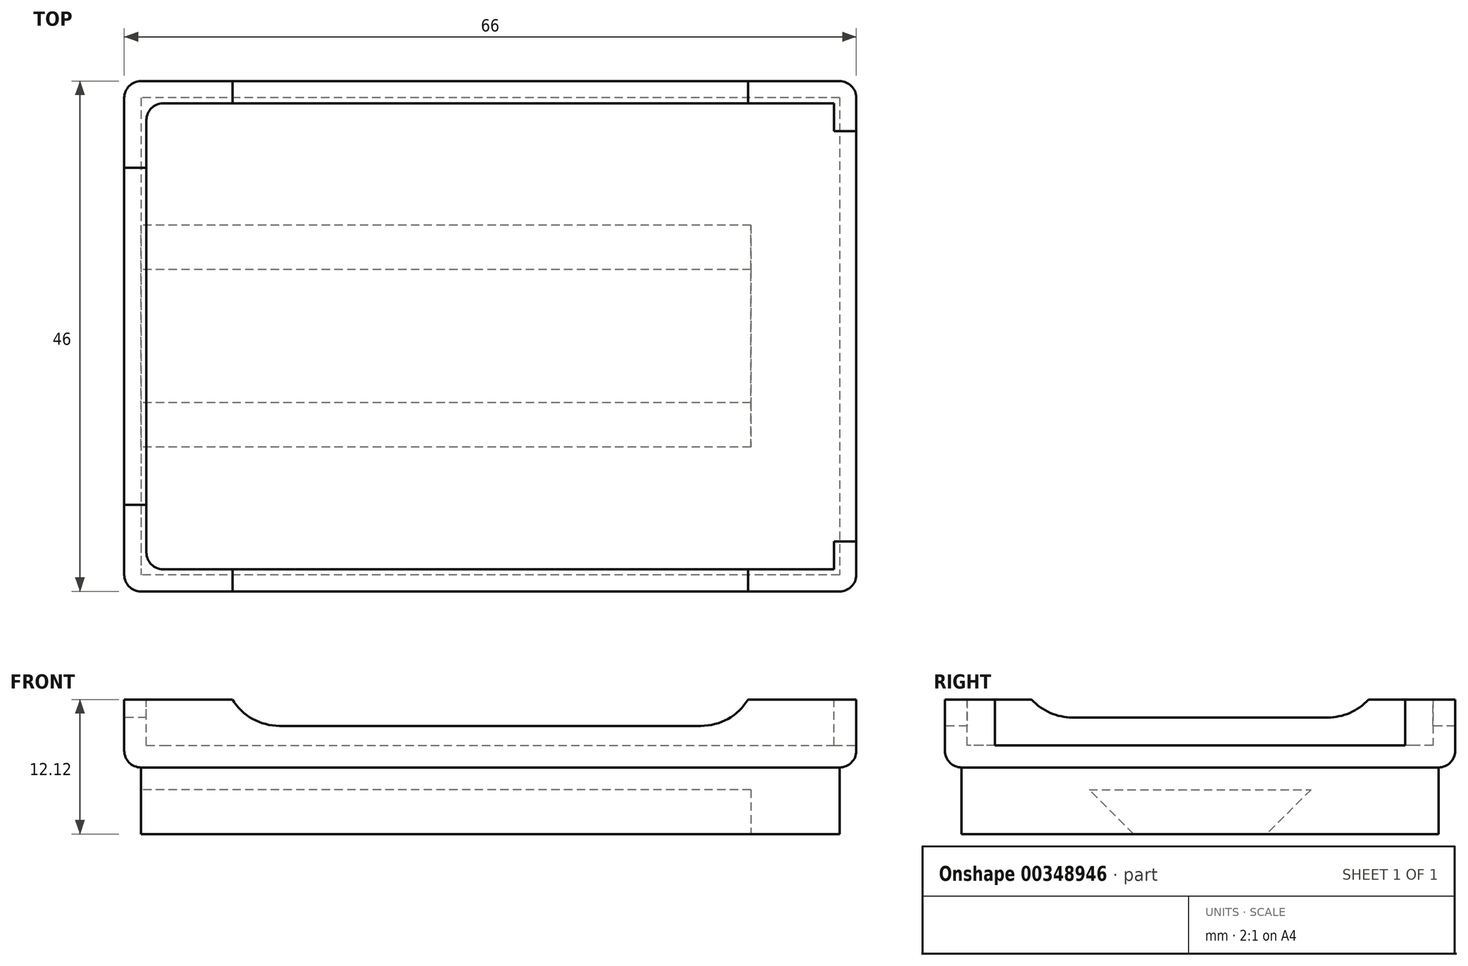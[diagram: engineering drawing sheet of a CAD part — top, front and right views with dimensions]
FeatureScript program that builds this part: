
annotation { "Feature Type Name" : "Feature", "Feature Type Description" : "" }
export const myFeature = defineFeature(function(context is Context, id is Id, definition is map)
    precondition{}
    {
        {
            var Q0;
            Q0=qCreatedBy(makeId("Top.planeOp"),FACE);
            var sketch = newSketch(context, id + "F0", { "sketchPlane" : qUnion([Q0])});
            skLineSegment(sketch, "E0.bottom", {"start": v(33, 23) * mm, "end": v(-33, 23) * mm});
            skLineSegment(sketch, "E0.top", {"start": v(33, -23) * mm, "end": v(-33, -23) * mm});
            skLineSegment(sketch, "E0.left", {"start": v(33, 23) * mm, "end": v(33, -23) * mm});
            skLineSegment(sketch, "E0.right", {"start": v(-33, 23) * mm, "end": v(-33, -23) * mm});
            skPoint(sketch, "E0.middle", {"position": v(0, 0) * mm});
            skSolve(sketch);
        }
        {
            var Q0;
            Q0=makeQuery(id+"F0.imprint","IMPRINT",FACE,{"disambiguationData":[TD([[makeQuery(id+"F0.imprint","IMPRINT",EDGE,{"derivedFrom":sQuery(id+"F0.wireOp",EDGE,"E0.bottom")}),1.0]])]});
            extrude(context, id + "F1", {"entities" : qUnion([Q0]), "depth" : 11.5 * mm});
        }
        {
            var Q0;
            Q0=makeQuery(id+"F1.opExtrude","CAP_EDGE",EDGE,{"disambiguationData":[OSD([sQuery(id+"F0.wireOp",EDGE,"E0.right")])],"isStart":false});
            var Q1;
            Q1=makeQuery(id+"F1.opExtrude","CAP_EDGE",EDGE,{"disambiguationData":[OSD([sQuery(id+"F0.wireOp",EDGE,"E0.top")])],"isStart":false});
            var Q2;
            Q2=makeQuery(id+"F1.opExtrude","CAP_EDGE",EDGE,{"disambiguationData":[OSD([sQuery(id+"F0.wireOp",EDGE,"E0.left")])],"isStart":false});
            var Q3;
            Q3=makeQuery(id+"F1.opExtrude","CAP_EDGE",EDGE,{"disambiguationData":[OSD([sQuery(id+"F0.wireOp",EDGE,"E0.bottom")])],"isStart":false});
            var Q4;
            Q4=makeQuery(id+"F1.opExtrude","SWEPT_EDGE",EDGE,{"disambiguationData":[OSD([sQuery(id+"F0.wireOp",EDGE,"E0.top"),sQuery(id+"F0.wireOp",EDGE,"E0.left")])]});
            var Q5;
            Q5=makeQuery(id+"F1.opExtrude","SWEPT_EDGE",EDGE,{"disambiguationData":[OSD([sQuery(id+"F0.wireOp",EDGE,"E0.bottom"),sQuery(id+"F0.wireOp",EDGE,"E0.left")])]});
            var Q6;
            Q6=makeQuery(id+"F1.opExtrude","SWEPT_EDGE",EDGE,{"disambiguationData":[OSD([sQuery(id+"F0.wireOp",EDGE,"E0.top"),sQuery(id+"F0.wireOp",EDGE,"E0.right")])]});
            var Q7;
            Q7=makeQuery(id+"F1.opExtrude","SWEPT_EDGE",EDGE,{"disambiguationData":[OSD([sQuery(id+"F0.wireOp",EDGE,"E0.bottom"),sQuery(id+"F0.wireOp",EDGE,"E0.right")])]});
            fillet(context, id + "F2", {"entities" : qUnion([Q0, Q1, Q2, Q3, Q4, Q5, Q6, Q7]), "radius" : 1.5 * mm, "tangentPropagation" : true, "allowEdgeOverflow" : false});
        }
        {
            var Q0;
            Q0=makeQuery(id+"F1.opExtrude","CAP_FACE",FACE,{"disambiguationData":[OSD([sQuery(id+"F0.wireOp",EDGE,"E0.bottom"),sQuery(id+"F0.wireOp",EDGE,"E0.top"),sQuery(id+"F0.wireOp",EDGE,"E0.left"),sQuery(id+"F0.wireOp",EDGE,"E0.right")])],"isStart":true});
            shell(context, id + "F3", {"entities" : qUnion([Q0]), "thickness" : 2 * mm});
        }
        {
            var Q0;
            Q0=makeQuery(id+"F3.opShell","OFFSET_EDGE",EDGE,{"disambiguationData":[OSD([sQuery(id+"F0.wireOp",EDGE,"E0.bottom"),sQuery(id+"F0.wireOp",EDGE,"E0.right")])]});
            var Q1;
            Q1=makeQuery(id+"F3.opShell","OFFSET_EDGE",EDGE,{"disambiguationData":[OSD([sQuery(id+"F0.wireOp",EDGE,"E0.top"),sQuery(id+"F0.wireOp",EDGE,"E0.right")])]});
            fillet(context, id + "F4", {"entities" : qUnion([Q0, Q1]), "radius" : 1.5 * mm, "tangentPropagation" : true, "allowEdgeOverflow" : false});
        }
        {
            var Q0;
            Q0=makeQuery(id+"F1.opExtrude","SWEPT_BODY",BODY,{"disambiguationData":[OSD([sQuery(id+"F0.wireOp",EDGE,"E0.bottom"),sQuery(id+"F0.wireOp",EDGE,"E0.top"),sQuery(id+"F0.wireOp",EDGE,"E0.left"),sQuery(id+"F0.wireOp",EDGE,"E0.right")])]});
            var Q1;
            Q1=qCreatedBy(makeId("Top.planeOp"),FACE);
            mirror(context, id + "F5", {"operationType" : NewBodyOperationType.ADD, "entities" : qUnion([Q0]), "mirrorPlane" : qUnion([Q1])});
        }
        {
            var Q0;
            {var subQ0=makeQuery(id+"F1.opExtrude","SWEPT_FACE",FACE,{"disambiguationData":[OSD([sQuery(id+"F0.wireOp",EDGE,"E0.top")])]});Q0=makeQuery(id+"F5.boolean.opBoolean","MERGE",FACE,{"derivedFrom":[subQ0,makeQuery(id+"F5.opPattern","COPY",FACE,{"derivedFrom":subQ0,"instanceName":"1"})]});}
            var sketch = newSketch(context, id + "F6", { "sketchPlane" : qUnion([Q0])});
            skLineSegment(sketch, "E1.bottom", {"start": v(24, -7.75) * mm, "end": v(-24, -7.75) * mm});
            skLineSegment(sketch, "E1.top", {"start": v(24, 7.75) * mm, "end": v(-24, 7.75) * mm});
            skLineSegment(sketch, "E1.left", {"start": v(24, -7.75) * mm, "end": v(24, 7.75) * mm});
            skLineSegment(sketch, "E1.right", {"start": v(-24, -7.75) * mm, "end": v(-24, 7.75) * mm});
            skPoint(sketch, "E1.middle", {"position": v(0, 0) * mm});
            skSolve(sketch);
        }
        {
            var Q0;
            Q0=makeQuery(id+"F6.imprint","IMPRINT",FACE,{"disambiguationData":[TD([[makeQuery(id+"F6.imprint","IMPRINT",EDGE,{"derivedFrom":sQuery(id+"F6.wireOp",EDGE,"E1.bottom")}),-1.0]])]});
            extrude(context, id + "F7", {"entities" : qUnion([Q0]), "operationType" : NewBodyOperationType.REMOVE, "endBound" : BoundingType.THROUGH_ALL, "oppositeDirection" : true, "depth" : 5 * mm});
        }
        {
            var Q0;
            {var subQ0=makeQuery(id+"F1.opExtrude","SWEPT_FACE",FACE,{"disambiguationData":[OSD([sQuery(id+"F0.wireOp",EDGE,"E0.right")])]});Q0=makeQuery(id+"F5.boolean.opBoolean","MERGE",FACE,{"derivedFrom":[subQ0,makeQuery(id+"F5.opPattern","COPY",FACE,{"derivedFrom":subQ0,"instanceName":"1"})]});}
            var sketch = newSketch(context, id + "F8", { "sketchPlane" : qUnion([Q0])});
            skLineSegment(sketch, "E2.bottom", {"start": v(16.5, 7) * mm, "end": v(-16.5, 7) * mm});
            skLineSegment(sketch, "E2.top", {"start": v(16.5, -7) * mm, "end": v(-16.5, -7) * mm});
            skLineSegment(sketch, "E2.left", {"start": v(16.5, 7) * mm, "end": v(16.5, -7) * mm});
            skLineSegment(sketch, "E2.right", {"start": v(-16.5, 7) * mm, "end": v(-16.5, -7) * mm});
            skPoint(sketch, "E2.middle", {"position": v(0, 0) * mm});
            skSolve(sketch);
        }
        {
            var Q0;
            Q0=makeQuery(id+"F8.imprint","IMPRINT",FACE,{"disambiguationData":[TD([[makeQuery(id+"F8.imprint","IMPRINT",EDGE,{"derivedFrom":sQuery(id+"F8.wireOp",EDGE,"E2.bottom")}),1.0]])]});
            extrude(context, id + "F9", {"entities" : qUnion([Q0]), "operationType" : NewBodyOperationType.REMOVE, "oppositeDirection" : true, "depth" : 5 * mm});
        }
        {
            var Q0;
            {var subQ0=sQuery(id+"F0.wireOp",EDGE,"E0.left");var subQ2=makeQuery(id+"F1.opExtrude","SWEPT_FACE",FACE,{"disambiguationData":[OSD([subQ0])]});var subQ3=sQuery(id+"F8.wireOp",EDGE,"E2.right");var subQ4=sQuery(id+"F8.wireOp",EDGE,"E2.top");Q0=makeQuery(id+"F9.boolean.opBoolean","COPY",EDGE,{"disambiguationData":[TD([subQ2])],"derivedFrom":makeQuery(id+"F9.opExtrude","SWEPT_EDGE",EDGE,{"disambiguationData":[OSD([subQ4,subQ3])]})});}
            var Q1;
            {var subQ0=sQuery(id+"F0.wireOp",EDGE,"E0.right");var subQ2=makeQuery(id+"F1.opExtrude","SWEPT_FACE",FACE,{"disambiguationData":[OSD([subQ0])]});var subQ3=sQuery(id+"F8.wireOp",EDGE,"E2.top");var subQ4=sQuery(id+"F8.wireOp",EDGE,"E2.right");Q1=makeQuery(id+"F9.boolean.opBoolean","COPY",EDGE,{"disambiguationData":[TD([subQ2])],"derivedFrom":makeQuery(id+"F9.opExtrude","SWEPT_EDGE",EDGE,{"disambiguationData":[OSD([subQ3,subQ4])]})});}
            var Q2;
            {var subQ0=sQuery(id+"F0.wireOp",EDGE,"E0.left");var subQ2=makeQuery(id+"F1.opExtrude","SWEPT_FACE",FACE,{"disambiguationData":[OSD([subQ0])]});var subQ3=sQuery(id+"F8.wireOp",EDGE,"E2.top");var subQ4=sQuery(id+"F8.wireOp",EDGE,"E2.left");Q2=makeQuery(id+"F9.boolean.opBoolean","COPY",EDGE,{"disambiguationData":[TD([subQ2])],"derivedFrom":makeQuery(id+"F9.opExtrude","SWEPT_EDGE",EDGE,{"disambiguationData":[OSD([subQ3,subQ4])]})});}
            var Q3;
            {var subQ0=sQuery(id+"F0.wireOp",EDGE,"E0.right");var subQ2=makeQuery(id+"F1.opExtrude","SWEPT_FACE",FACE,{"disambiguationData":[OSD([subQ0])]});var subQ3=sQuery(id+"F8.wireOp",EDGE,"E2.top");var subQ4=sQuery(id+"F8.wireOp",EDGE,"E2.left");Q3=makeQuery(id+"F9.boolean.opBoolean","COPY",EDGE,{"disambiguationData":[TD([subQ2])],"derivedFrom":makeQuery(id+"F9.opExtrude","SWEPT_EDGE",EDGE,{"disambiguationData":[OSD([subQ3,subQ4])]})});}
            var Q4;
            {var subQ0=sQuery(id+"F0.wireOp",EDGE,"E0.left");var subQ2=makeQuery(id+"F1.opExtrude","SWEPT_FACE",FACE,{"disambiguationData":[OSD([subQ0])]});var subQ3=sQuery(id+"F8.wireOp",EDGE,"E2.right");var subQ4=sQuery(id+"F8.wireOp",EDGE,"E2.bottom");Q4=makeQuery(id+"F9.boolean.opBoolean","COPY",EDGE,{"disambiguationData":[TD([subQ2])],"derivedFrom":makeQuery(id+"F9.opExtrude","SWEPT_EDGE",EDGE,{"disambiguationData":[OSD([subQ4,subQ3])]})});}
            var Q5;
            {var subQ0=sQuery(id+"F0.wireOp",EDGE,"E0.right");var subQ2=makeQuery(id+"F1.opExtrude","SWEPT_FACE",FACE,{"disambiguationData":[OSD([subQ0])]});var subQ3=sQuery(id+"F8.wireOp",EDGE,"E2.bottom");var subQ4=sQuery(id+"F8.wireOp",EDGE,"E2.right");Q5=makeQuery(id+"F9.boolean.opBoolean","COPY",EDGE,{"disambiguationData":[TD([subQ2])],"derivedFrom":makeQuery(id+"F9.opExtrude","SWEPT_EDGE",EDGE,{"disambiguationData":[OSD([subQ3,subQ4])]})});}
            var Q6;
            {var subQ0=sQuery(id+"F0.wireOp",EDGE,"E0.right");var subQ2=sQuery(id+"F8.wireOp",EDGE,"E2.bottom");var subQ3=makeQuery(id+"F1.opExtrude","SWEPT_FACE",FACE,{"disambiguationData":[OSD([subQ0])]});var subQ4=sQuery(id+"F8.wireOp",EDGE,"E2.left");Q6=makeQuery(id+"F9.boolean.opBoolean","COPY",EDGE,{"disambiguationData":[TD([subQ3])],"derivedFrom":makeQuery(id+"F9.opExtrude","SWEPT_EDGE",EDGE,{"disambiguationData":[OSD([subQ2,subQ4])]})});}
            var Q7;
            {var subQ0=sQuery(id+"F0.wireOp",EDGE,"E0.left");var subQ2=makeQuery(id+"F1.opExtrude","SWEPT_FACE",FACE,{"disambiguationData":[OSD([subQ0])]});var subQ3=sQuery(id+"F8.wireOp",EDGE,"E2.bottom");var subQ4=sQuery(id+"F8.wireOp",EDGE,"E2.left");Q7=makeQuery(id+"F9.boolean.opBoolean","COPY",EDGE,{"disambiguationData":[TD([subQ2])],"derivedFrom":makeQuery(id+"F9.opExtrude","SWEPT_EDGE",EDGE,{"disambiguationData":[OSD([subQ3,subQ4])]})});}
            fillet(context, id + "F10", {"entities" : qUnion([Q0, Q1, Q2, Q3, Q4, Q5, Q6, Q7]), "radius" : 5 * mm, "tangentPropagation" : true, "allowEdgeOverflow" : false});
        }
        {
            var Q0;
            {var subQ0=sQuery(id+"F0.wireOp",EDGE,"E0.top");var subQ2=makeQuery(id+"F1.opExtrude","SWEPT_FACE",FACE,{"disambiguationData":[OSD([subQ0])]});var subQ3=sQuery(id+"F6.wireOp",EDGE,"E1.top");var subQ4=sQuery(id+"F6.wireOp",EDGE,"E1.right");Q0=makeQuery(id+"F7.boolean.opBoolean","COPY",EDGE,{"disambiguationData":[TD([subQ2])],"derivedFrom":makeQuery(id+"F7.opExtrude","SWEPT_EDGE",EDGE,{"disambiguationData":[OSD([subQ3,subQ4])]})});}
            var Q1;
            {var subQ0=sQuery(id+"F0.wireOp",EDGE,"E0.top");var subQ2=makeQuery(id+"F1.opExtrude","SWEPT_FACE",FACE,{"disambiguationData":[OSD([subQ0])]});var subQ3=sQuery(id+"F6.wireOp",EDGE,"E1.left");var subQ4=sQuery(id+"F6.wireOp",EDGE,"E1.top");Q1=makeQuery(id+"F7.boolean.opBoolean","COPY",EDGE,{"disambiguationData":[TD([subQ2])],"derivedFrom":makeQuery(id+"F7.opExtrude","SWEPT_EDGE",EDGE,{"disambiguationData":[OSD([subQ4,subQ3])]})});}
            var Q2;
            {var subQ0=sQuery(id+"F0.wireOp",EDGE,"E0.top");var subQ2=sQuery(id+"F6.wireOp",EDGE,"E1.bottom");var subQ3=makeQuery(id+"F1.opExtrude","SWEPT_FACE",FACE,{"disambiguationData":[OSD([subQ0])]});var subQ4=sQuery(id+"F6.wireOp",EDGE,"E1.right");Q2=makeQuery(id+"F7.boolean.opBoolean","COPY",EDGE,{"disambiguationData":[TD([subQ3])],"derivedFrom":makeQuery(id+"F7.opExtrude","SWEPT_EDGE",EDGE,{"disambiguationData":[OSD([subQ2,subQ4])]})});}
            var Q3;
            {var subQ0=sQuery(id+"F0.wireOp",EDGE,"E0.top");var subQ2=sQuery(id+"F6.wireOp",EDGE,"E1.bottom");var subQ3=makeQuery(id+"F1.opExtrude","SWEPT_FACE",FACE,{"disambiguationData":[OSD([subQ0])]});var subQ4=sQuery(id+"F6.wireOp",EDGE,"E1.left");Q3=makeQuery(id+"F7.boolean.opBoolean","COPY",EDGE,{"disambiguationData":[TD([subQ3])],"derivedFrom":makeQuery(id+"F7.opExtrude","SWEPT_EDGE",EDGE,{"disambiguationData":[OSD([subQ2,subQ4])]})});}
            fillet(context, id + "F11", {"entities" : qUnion([Q0, Q1, Q2, Q3]), "radius" : 5 * mm, "tangentPropagation" : true, "allowEdgeOverflow" : false});
        }
        {
            var Q0;
            {var subQ0=sQuery(id+"F0.wireOp",EDGE,"E0.bottom");var subQ1=makeQuery(id+"F1.opExtrude","SWEPT_FACE",FACE,{"disambiguationData":[OSD([subQ0])]});var subQ3=sQuery(id+"F6.wireOp",EDGE,"E1.top");var subQ4=sQuery(id+"F6.wireOp",EDGE,"E1.left");Q0=makeQuery(id+"F7.boolean.opBoolean","COPY",EDGE,{"disambiguationData":[TD([subQ1])],"derivedFrom":makeQuery(id+"F7.opExtrude","SWEPT_EDGE",EDGE,{"disambiguationData":[OSD([subQ3,subQ4])]})});}
            var Q1;
            {var subQ0=sQuery(id+"F0.wireOp",EDGE,"E0.bottom");var subQ1=makeQuery(id+"F1.opExtrude","SWEPT_FACE",FACE,{"disambiguationData":[OSD([subQ0])]});var subQ3=sQuery(id+"F6.wireOp",EDGE,"E1.bottom");var subQ4=sQuery(id+"F6.wireOp",EDGE,"E1.left");Q1=makeQuery(id+"F7.boolean.opBoolean","COPY",EDGE,{"disambiguationData":[TD([subQ1])],"derivedFrom":makeQuery(id+"F7.opExtrude","SWEPT_EDGE",EDGE,{"disambiguationData":[OSD([subQ3,subQ4])]})});}
            var Q2;
            {var subQ0=sQuery(id+"F0.wireOp",EDGE,"E0.bottom");var subQ1=makeQuery(id+"F1.opExtrude","SWEPT_FACE",FACE,{"disambiguationData":[OSD([subQ0])]});var subQ3=sQuery(id+"F6.wireOp",EDGE,"E1.right");var subQ4=sQuery(id+"F6.wireOp",EDGE,"E1.bottom");Q2=makeQuery(id+"F7.boolean.opBoolean","COPY",EDGE,{"disambiguationData":[TD([subQ1])],"derivedFrom":makeQuery(id+"F7.opExtrude","SWEPT_EDGE",EDGE,{"disambiguationData":[OSD([subQ4,subQ3])]})});}
            var Q3;
            {var subQ0=sQuery(id+"F0.wireOp",EDGE,"E0.bottom");var subQ1=makeQuery(id+"F1.opExtrude","SWEPT_FACE",FACE,{"disambiguationData":[OSD([subQ0])]});var subQ3=sQuery(id+"F6.wireOp",EDGE,"E1.right");var subQ4=sQuery(id+"F6.wireOp",EDGE,"E1.top");Q3=makeQuery(id+"F7.boolean.opBoolean","COPY",EDGE,{"disambiguationData":[TD([subQ1])],"derivedFrom":makeQuery(id+"F7.opExtrude","SWEPT_EDGE",EDGE,{"disambiguationData":[OSD([subQ4,subQ3])]})});}
            fillet(context, id + "F12", {"entities" : qUnion([Q0, Q1, Q2, Q3]), "radius" : 5 * mm, "tangentPropagation" : true, "allowEdgeOverflow" : false});
        }
        {
            var Q0;
            Q0=makeQuery(id+"F1.opExtrude","CAP_FACE",FACE,{"disambiguationData":[OSD([sQuery(id+"F0.wireOp",EDGE,"E0.bottom"),sQuery(id+"F0.wireOp",EDGE,"E0.top"),sQuery(id+"F0.wireOp",EDGE,"E0.left"),sQuery(id+"F0.wireOp",EDGE,"E0.right")])],"isStart":false});
            var sketch = newSketch(context, id + "F13", { "sketchPlane" : qUnion([Q0])});
            skLineSegment(sketch, "E3.bottom", {"start": v(20, -10) * mm, "end": v(-20, -10) * mm});
            skLineSegment(sketch, "E3.top", {"start": v(20, 10) * mm, "end": v(-20, 10) * mm});
            skLineSegment(sketch, "E3.left", {"start": v(20, -10) * mm, "end": v(20, 10) * mm});
            skLineSegment(sketch, "E3.right", {"start": v(-20, -10) * mm, "end": v(-20, 10) * mm});
            skPoint(sketch, "E3.middle", {"position": v(0, 0) * mm});
            skSolve(sketch);
        }
        {
            var Q0;
            Q0=makeQuery(id+"F13.imprint","IMPRINT",FACE,{"disambiguationData":[TD([[makeQuery(id+"F13.imprint","IMPRINT",EDGE,{"derivedFrom":sQuery(id+"F13.wireOp",EDGE,"E3.bottom")}),-1.0]])]});
            extrude(context, id + "F14", {"entities" : qUnion([Q0]), "operationType" : NewBodyOperationType.REMOVE, "oppositeDirection" : true, "depth" : 5 * mm});
        }
        {
            var Q0;
            Q0=makeQuery(id+"F14.boolean.opBoolean","COPY",EDGE,{"derivedFrom":makeQuery(id+"F14.opExtrude","SWEPT_EDGE",EDGE,{"disambiguationData":[OSD([sQuery(id+"F13.wireOp",EDGE,"E3.top"),sQuery(id+"F13.wireOp",EDGE,"E3.right")])]})});
            var Q1;
            Q1=makeQuery(id+"F14.boolean.opBoolean","COPY",EDGE,{"derivedFrom":makeQuery(id+"F14.opExtrude","SWEPT_EDGE",EDGE,{"disambiguationData":[OSD([sQuery(id+"F13.wireOp",EDGE,"E3.bottom"),sQuery(id+"F13.wireOp",EDGE,"E3.right")])]})});
            var Q2;
            Q2=makeQuery(id+"F14.boolean.opBoolean","COPY",EDGE,{"derivedFrom":makeQuery(id+"F14.opExtrude","SWEPT_EDGE",EDGE,{"disambiguationData":[OSD([sQuery(id+"F13.wireOp",EDGE,"E3.bottom"),sQuery(id+"F13.wireOp",EDGE,"E3.left")])]})});
            var Q3;
            Q3=makeQuery(id+"F14.boolean.opBoolean","COPY",EDGE,{"derivedFrom":makeQuery(id+"F14.opExtrude","SWEPT_EDGE",EDGE,{"disambiguationData":[OSD([sQuery(id+"F13.wireOp",EDGE,"E3.top"),sQuery(id+"F13.wireOp",EDGE,"E3.left")])]})});
            fillet(context, id + "F15", {"entities" : qUnion([Q0, Q1, Q2, Q3]), "radius" : 5 * mm, "tangentPropagation" : true, "allowEdgeOverflow" : false});
        }
        {
            var Q0;
            {var subQ0=makeQuery(id+"F1.opExtrude","SWEPT_FACE",FACE,{"disambiguationData":[OSD([sQuery(id+"F0.wireOp",EDGE,"E0.left")])]});Q0=makeQuery(id+"F5.boolean.opBoolean","MERGE",FACE,{"derivedFrom":[subQ0,makeQuery(id+"F5.opPattern","COPY",FACE,{"derivedFrom":subQ0,"instanceName":"1"})]});}
            var sketch = newSketch(context, id + "F16", { "sketchPlane" : qUnion([Q0])});
            skLineSegment(sketch, "E4.bottom", {"start": v(18.5, -9.5) * mm, "end": v(-18.5, -9.5) * mm});
            skLineSegment(sketch, "E4.top", {"start": v(18.5, 9.5) * mm, "end": v(-18.5, 9.5) * mm});
            skLineSegment(sketch, "E4.left", {"start": v(18.5, -9.5) * mm, "end": v(18.5, 9.5) * mm});
            skLineSegment(sketch, "E4.right", {"start": v(-18.5, -9.5) * mm, "end": v(-18.5, 9.5) * mm});
            skPoint(sketch, "E4.middle", {"position": v(0, 0) * mm});
            skSolve(sketch);
        }
        {
            var Q0;
            Q0=makeQuery(id+"F16.imprint","IMPRINT",FACE,{"disambiguationData":[TD([[makeQuery(id+"F16.imprint","IMPRINT",EDGE,{"derivedFrom":sQuery(id+"F16.wireOp",EDGE,"E4.bottom")}),-1.0]])]});
            extrude(context, id + "F17", {"entities" : qUnion([Q0]), "operationType" : NewBodyOperationType.REMOVE, "oppositeDirection" : true, "depth" : 5 * mm});
        }
        {
            var Q0;
            Q0=makeQuery(id+"F5.opPattern","COPY",FACE,{"derivedFrom":makeQuery(id+"F1.opExtrude","CAP_FACE",FACE,{"disambiguationData":[OSD([sQuery(id+"F0.wireOp",EDGE,"E0.bottom"),sQuery(id+"F0.wireOp",EDGE,"E0.top"),sQuery(id+"F0.wireOp",EDGE,"E0.left"),sQuery(id+"F0.wireOp",EDGE,"E0.right")])],"isStart":false}),"instanceName":"1"});
            var sketch = newSketch(context, id + "F18", { "sketchPlane" : qUnion([Q0])});
            skLineSegment(sketch, "E5.bottom", {"start": v(31.5, -21.5) * mm, "end": v(-31.5, -21.5) * mm});
            skLineSegment(sketch, "E5.top", {"start": v(31.5, 21.5) * mm, "end": v(-31.5, 21.5) * mm});
            skLineSegment(sketch, "E5.left", {"start": v(31.5, -21.5) * mm, "end": v(31.5, 21.5) * mm});
            skLineSegment(sketch, "E5.right", {"start": v(-31.5, -21.5) * mm, "end": v(-31.5, 21.5) * mm});
            skPoint(sketch, "E5.middle", {"position": v(0, 0) * mm});
            skSolve(sketch);
        }
        {
            var Q0;
            Q0=makeQuery(id+"F18.imprint","IMPRINT",FACE,{"disambiguationData":[TD([[makeQuery(id+"F18.imprint","IMPRINT",EDGE,{"derivedFrom":sQuery(id+"F18.wireOp",EDGE,"E5.bottom")}),-1.0]])]});
            extrude(context, id + "F19", {"entities" : qUnion([Q0]), "operationType" : NewBodyOperationType.ADD, "depth" : 6 * mm});
        }
        {
            var Q0;
            Q0=makeQuery(id+"F19.opExtrude","SWEPT_FACE",FACE,{"disambiguationData":[OSD([sQuery(id+"F18.wireOp",EDGE,"E5.right")])]});
            var sketch = newSketch(context, id + "F20", { "sketchPlane" : qUnion([Q0])});
            skLineSegment(sketch, "E6.bottom", {"start": v(10, -21.5) * mm, "end": v(-10, -21.5) * mm, "construction": true});
            skLineSegment(sketch, "E6.top", {"start": v(10, -13.5) * mm, "end": v(-10, -13.5) * mm, "construction": true});
            skLineSegment(sketch, "E6.left", {"start": v(10, -21.5) * mm, "end": v(10, -13.5) * mm, "construction": true});
            skLineSegment(sketch, "E6.right", {"start": v(-10, -21.5) * mm, "end": v(-10, -13.5) * mm, "construction": true});
            skPoint(sketch, "E6.middle", {"position": v(0, -17.5) * mm});
            skLineSegment(sketch, "E7.bottom", {"start": v(6, -21.5) * mm, "end": v(-6, -21.5) * mm, "construction": true});
            skLineSegment(sketch, "E7.top", {"start": v(6, -13.5) * mm, "end": v(-6, -13.5) * mm, "construction": true});
            skLineSegment(sketch, "E7.left", {"start": v(6, -21.5) * mm, "end": v(6, -13.5) * mm, "construction": true});
            skLineSegment(sketch, "E7.right", {"start": v(-6, -21.5) * mm, "end": v(-6, -13.5) * mm, "construction": true});
            skPoint(sketch, "E8", {"position": v(-6, -17.5) * mm});
            skPoint(sketch, "E9", {"position": v(6, -17.5) * mm});
            skLineSegment(sketch, "E10", {"start": v(6, -17.5) * mm, "end": v(-6, -17.5) * mm, "construction": true});
            skLineSegment(sketch, "E11", {"start": v(6, -17.5) * mm, "end": v(-6, -17.5) * mm});
            skLineSegment(sketch, "E12", {"start": v(-10, -13.5) * mm, "end": v(-6, -17.5) * mm});
            skLineSegment(sketch, "E13", {"start": v(6, -17.5) * mm, "end": v(10, -13.5) * mm});
            skLineSegment(sketch, "E14", {"start": v(10, -13.5) * mm, "end": v(-10, -13.5) * mm});
            skSolve(sketch);
        }
        {
            var Q0;
            Q0=makeQuery(id+"F20.imprint","IMPRINT",FACE,{"disambiguationData":[TD([[makeQuery(id+"F20.imprint","IMPRINT",EDGE,{"derivedFrom":sQuery(id+"F20.wireOp",EDGE,"E11")}),1.0]])]});
            extrude(context, id + "F21", {"entities" : qUnion([Q0]), "operationType" : NewBodyOperationType.REMOVE, "oppositeDirection" : true, "depth" : 55 * mm});
        }
        {
            var Q0;
            Q0=qCreatedBy(makeId("Right.planeOp"),FACE);
            var sketch = newSketch(context, id + "F22", { "sketchPlane" : qUnion([Q0])});
            skLineSegment(sketch, "E15.bottom", {"start": v(-25.04, -5.38) * mm, "end": v(24.96, -5.38) * mm});
            skLineSegment(sketch, "E15.top", {"start": v(-25.04, 14.62) * mm, "end": v(24.96, 14.62) * mm});
            skLineSegment(sketch, "E15.left", {"start": v(-25.04, -5.38) * mm, "end": v(-25.04, 14.62) * mm});
            skLineSegment(sketch, "E15.right", {"start": v(24.96, -5.38) * mm, "end": v(24.96, 14.62) * mm});
            skSolve(sketch);
        }
        {
            var Q0;
            Q0=makeQuery(id+"F22.imprint","IMPRINT",FACE,{"disambiguationData":[TD([[makeQuery(id+"F22.imprint","IMPRINT",EDGE,{"derivedFrom":sQuery(id+"F22.wireOp",EDGE,"E15.bottom")}),1.0]])]});
            extrude(context, id + "F23", {"entities" : qUnion([Q0]), "operationType" : NewBodyOperationType.REMOVE, "endBound" : BoundingType.SYMMETRIC, "depth" : 66 * mm});
        }
    });
